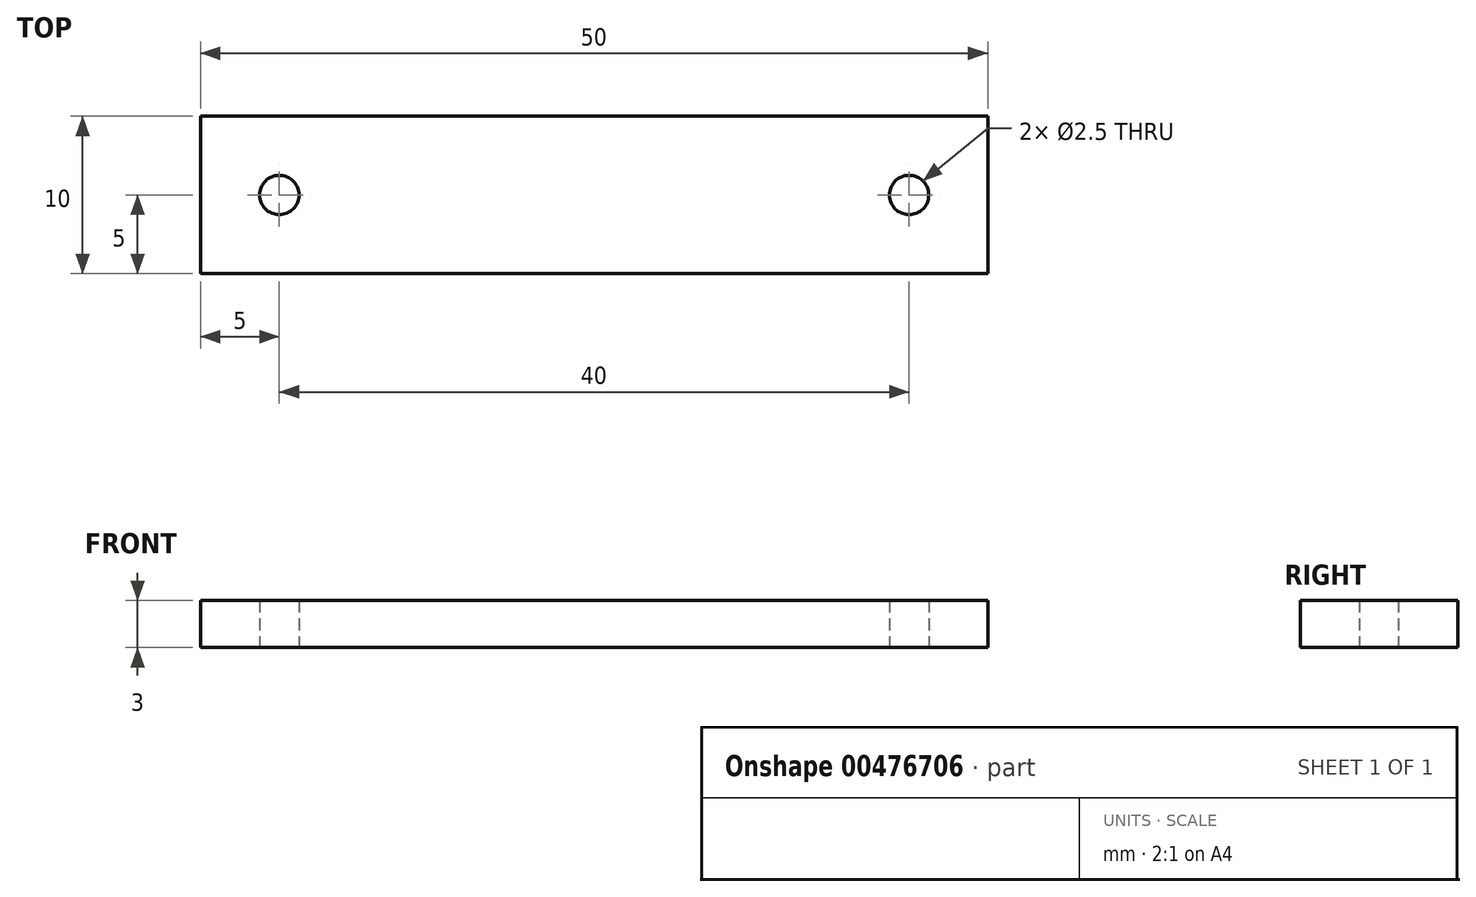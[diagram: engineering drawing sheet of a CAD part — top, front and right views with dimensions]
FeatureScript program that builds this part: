
annotation { "Feature Type Name" : "Feature", "Feature Type Description" : "" }
export const myFeature = defineFeature(function(context is Context, id is Id, definition is map)
    precondition{}
    {
        {
            var Q0;
            Q0=qCreatedBy(makeId("Top.planeOp"),FACE);
            var sketch = newSketch(context, id + "F0", { "sketchPlane" : qUnion([Q0])});
            skLineSegment(sketch, "E0.bottom", {"start": v(-25, 5) * mm, "end": v(25, 5) * mm});
            skLineSegment(sketch, "E0.top", {"start": v(-25, -5) * mm, "end": v(25, -5) * mm});
            skLineSegment(sketch, "E0.left", {"start": v(-25, 5) * mm, "end": v(-25, -5) * mm});
            skLineSegment(sketch, "E0.right", {"start": v(25, 5) * mm, "end": v(25, -5) * mm});
            skPoint(sketch, "E0.middle", {"position": v(0, 0) * mm});
            skCircle(sketch, "E1", {"center": v(-20, 0) * mm, "radius": 1.25 * mm});
            skCircle(sketch, "E2", {"center": v(20, 0) * mm, "radius": 1.25 * mm});
            skCircle(sketch, "E3", {"center": v(0, -10) * mm, "radius": 5 * mm});
            skPoint(sketch, "E3.centerSnap0", {"position": v(0, -5) * mm});
            skLineSegment(sketch, "E4", {"start": v(5, -9.98) * mm, "end": v(5, -5) * mm});
            skLineSegment(sketch, "E5", {"start": v(-5, -5) * mm, "end": v(-5, -10) * mm});
            skSolve(sketch);
        }
        {
            var Q0;
            Q0=makeQuery(id+"F0.imprint","IMPRINT",FACE,{"disambiguationData":[TD([[makeQuery(id+"F0.imprint","IMPRINT",EDGE,{"derivedFrom":sQuery(id+"F0.wireOp",EDGE,"E0.bottom")}),-1.0]])]});
            extrude(context, id + "F1", {"entities" : qUnion([Q0]), "depth" : 3 * mm});
        }
    });
